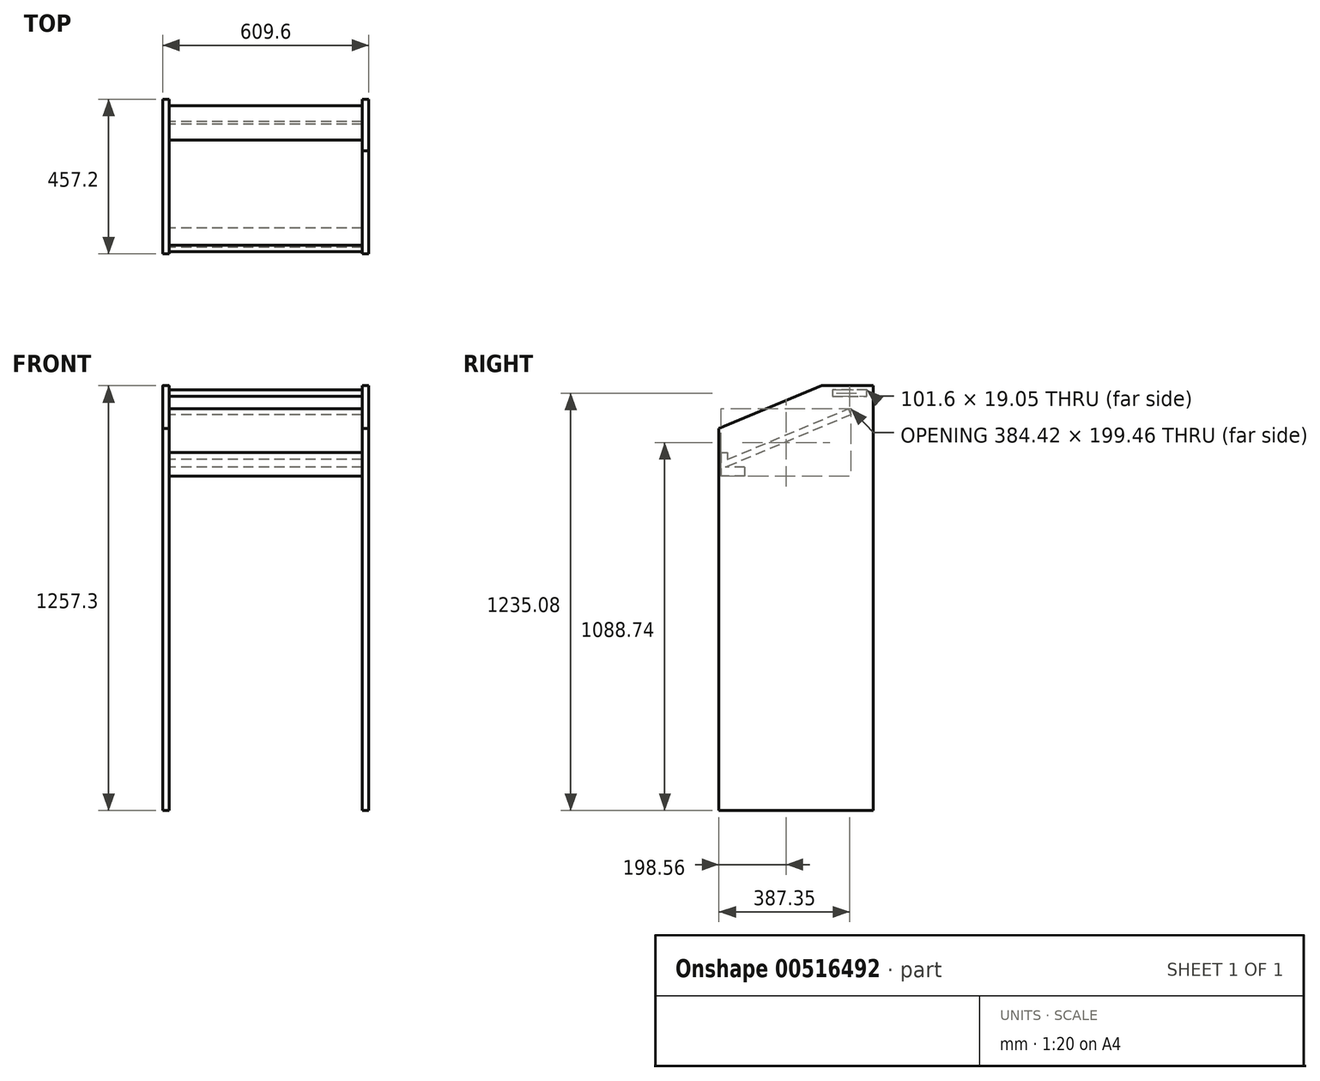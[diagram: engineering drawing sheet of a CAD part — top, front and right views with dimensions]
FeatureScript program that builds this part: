
annotation { "Feature Type Name" : "Feature", "Feature Type Description" : "" }
export const myFeature = defineFeature(function(context is Context, id is Id, definition is map)
    precondition{}
    {
        {
            var Q0;
            Q0=qCreatedBy(makeId("Right.planeOp"),FACE);
            var sketch = newSketch(context, id + "F0", { "sketchPlane" : qUnion([Q0])});
            skLineSegment(sketch, "E0.bottom", {"start": v(228.6, 628.65) * mm, "end": v(-228.6, 628.65) * mm});
            skLineSegment(sketch, "E0.top", {"start": v(228.6, -628.65) * mm, "end": v(-228.6, -628.65) * mm});
            skLineSegment(sketch, "E0.left", {"start": v(228.6, 628.65) * mm, "end": v(228.6, -628.65) * mm});
            skLineSegment(sketch, "E0.right", {"start": v(-228.6, 628.65) * mm, "end": v(-228.6, -628.65) * mm});
            skPoint(sketch, "E0.middle", {"position": v(0, 0) * mm});
            skLineSegment(sketch, "E1", {"start": v(-228.6, -628.65) * mm, "end": v(-228.6, 501.65) * mm});
            skLineSegment(sketch, "E2", {"start": v(228.6, 628.65) * mm, "end": v(81.28, 628.65) * mm});
            skLineSegment(sketch, "E3", {"start": v(71.51, 626.7) * mm, "end": v(-228.6, 501.65) * mm});
            skPoint(sketch, "E4.visualSharp", {"position": v(76.2, 628.65) * mm});
            skArc(sketch, "E4.filletArc", {"start": v(81.28, 628.65) * mm, "mid": v(76.3, 628.16) * mm, "end": v(71.51, 626.7) * mm});
            skSolve(sketch);
        }
        {
            var Q0;
            Q0=makeQuery(id+"F0.imprint","IMPRINT",FACE,{"disambiguationData":[TD([[makeQuery(id+"F0.imprint","IMPRINT",EDGE,{"derivedFrom":sQuery(id+"F0.wireOp",EDGE,"E0.top")}),-1.0]])]});
            extrude(context, id + "F1", {"entities" : qUnion([Q0]), "depth" : 19.05 * mm, "offsetDistance" : 25.4 * mm});
        }
        {
            var Q0;
            Q0=makeQuery(id+"F1.opExtrude","CAP_FACE",FACE,{"disambiguationData":[OSD([sQuery(id+"F0.wireOp",EDGE,"E0.top"),sQuery(id+"F0.wireOp",EDGE,"E0.left"),sQuery(id+"F0.wireOp",EDGE,"E1"),sQuery(id+"F0.wireOp",EDGE,"E2"),sQuery(id+"F0.wireOp",EDGE,"E3"),sQuery(id+"F0.wireOp",EDGE,"E4.filletArc")])],"isStart":false});
            var sketch = newSketch(context, id + "F2", { "sketchPlane" : qUnion([Q0])});
            skLineSegment(sketch, "E5", {"start": v(228.6, 628.65) * mm, "end": v(209.55, 628.65) * mm});
            skLineSegment(sketch, "E6", {"start": v(209.55, 615.95) * mm, "end": v(107.95, 615.95) * mm});
            skLineSegment(sketch, "E7", {"start": v(107.95, 615.95) * mm, "end": v(107.95, 596.9) * mm});
            skLineSegment(sketch, "E8", {"start": v(107.95, 596.9) * mm, "end": v(209.55, 596.9) * mm});
            skLineSegment(sketch, "E9", {"start": v(209.55, 596.9) * mm, "end": v(209.55, 615.95) * mm});
            skSolve(sketch);
        }
        {
            var Q0;
            Q0=makeQuery(id+"F2.imprint","IMPRINT",FACE,{"disambiguationData":[TD([[makeQuery(id+"F2.imprint","IMPRINT",EDGE,{"derivedFrom":sQuery(id+"F2.wireOp",EDGE,"E6")}),1.0]])]});
            extrude(context, id + "F3", {"entities" : qUnion([Q0]), "operationType" : NewBodyOperationType.ADD, "depth" : 571.5 * mm, "offsetDistance" : 25.4 * mm});
        }
        {
            var Q0;
            Q0=makeQuery(id+"F1.opExtrude","CAP_FACE",FACE,{"disambiguationData":[OSD([sQuery(id+"F0.wireOp",EDGE,"E0.top"),sQuery(id+"F0.wireOp",EDGE,"E0.left"),sQuery(id+"F0.wireOp",EDGE,"E1"),sQuery(id+"F0.wireOp",EDGE,"E2"),sQuery(id+"F0.wireOp",EDGE,"E3"),sQuery(id+"F0.wireOp",EDGE,"E4.filletArc")])],"isStart":false});
            var sketch = newSketch(context, id + "F4", { "sketchPlane" : qUnion([Q0])});
            skLineSegment(sketch, "E10", {"start": v(-228.6, 501.65) * mm, "end": v(-228.6, 400.05) * mm});
            skLineSegment(sketch, "E11", {"start": v(-228.6, 400.05) * mm, "end": v(107.95, 540.28) * mm});
            skLineSegment(sketch, "E12", {"start": v(107.95, 540.28) * mm, "end": v(154.84, 559.82) * mm});
            skLineSegment(sketch, "E13", {"start": v(154.84, 559.82) * mm, "end": v(162.17, 542.23) * mm});
            skLineSegment(sketch, "E14", {"start": v(162.17, 542.23) * mm, "end": v(-228.6, 379.41) * mm});
            skLineSegment(sketch, "E15", {"start": v(-228.6, 379.41) * mm, "end": v(-228.6, 430.21) * mm});
            skLineSegment(sketch, "E16", {"start": v(-228.6, 430.21) * mm, "end": v(-209.55, 430.21) * mm});
            skLineSegment(sketch, "E17", {"start": v(-209.55, 430.21) * mm, "end": v(-209.55, 379.41) * mm});
            skLineSegment(sketch, "E18", {"start": v(-209.55, 379.41) * mm, "end": v(-228.6, 379.41) * mm});
            skSolve(sketch);
        }
        {
            var Q0;
            {var subQ5=sQuery(id+"F4.wireOp",EDGE,"E16");Q0=makeQuery(id+"F4.imprint","IMPRINT",FACE,{"disambiguationData":[TD([[makeQuery(id+"F4.imprint","IMPRINT",EDGE,{"derivedFrom":subQ5}),-1.0]])]});}
            var Q1;
            {var subQ0=sQuery(id+"F4.wireOp",EDGE,"E15");var subQ1=sQuery(id+"F4.wireOp",EDGE,"E11");var subQ2=makeQuery(id+"F4.imprint","INTERSECT",VERTEX,{"derivedFrom":[subQ1,subQ0]});Q1=makeQuery(id+"F4.imprint","IMPRINT",FACE,{"disambiguationData":[TD([[makeQuery(id+"F4.imprint","IMPRINT",EDGE,{"disambiguationData":[TD([[subQ2,-1.0]])],"derivedFrom":subQ1}),-1.0]])]});}
            var Q2;
            {var subQ0=sQuery(id+"F4.wireOp",EDGE,"E18");Q2=makeQuery(id+"F4.imprint","IMPRINT",FACE,{"disambiguationData":[TD([[makeQuery(id+"F4.imprint","IMPRINT",EDGE,{"derivedFrom":subQ0}),-1.0]])]});}
            var Q3;
            {var subQ4=sQuery(id+"F4.wireOp",EDGE,"E12");Q3=makeQuery(id+"F4.imprint","IMPRINT",FACE,{"disambiguationData":[TD([[makeQuery(id+"F4.imprint","IMPRINT",EDGE,{"derivedFrom":subQ4}),-1.0]])]});}
            extrude(context, id + "F5", {"entities" : qUnion([Q0, Q1, Q2, Q3]), "operationType" : NewBodyOperationType.ADD, "depth" : 571.5 * mm, "offsetDistance" : 25.4 * mm});
        }
        {
            var Q0;
            Q0=makeQuery(id+"F5.boolean.opBoolean","MERGE",FACE,{"derivedFrom":[makeQuery(id+"F1.opExtrude","SWEPT_FACE",FACE,{"disambiguationData":[OSD([sQuery(id+"F0.wireOp",EDGE,"E1")])]}),makeQuery(id+"F5.opExtrude","SWEPT_FACE",FACE,{"disambiguationData":[OSD([sQuery(id+"F4.wireOp",EDGE,"E15")])]})]});
            var sketch = newSketch(context, id + "F6", { "sketchPlane" : qUnion([Q0])});
            skLineSegment(sketch, "E19", {"start": v(19.05, 430.21) * mm, "end": v(19.05, 379.41) * mm});
            skSolve(sketch);
        }
        {
            var Q0;
            Q0=makeQuery(id+"F6.imprint","IMPRINT",FACE,{"disambiguationData":[TD([[makeQuery(id+"F6.imprint","IMPRINT",EDGE,{"derivedFrom":sQuery(id+"F6.wireOp",EDGE,"E19")}),1.0]])]});
            extrude(context, id + "F7", {"entities" : qUnion([Q0]), "operationType" : NewBodyOperationType.REMOVE, "oppositeDirection" : true, "depth" : 6.35 * mm, "offsetDistance" : 25.4 * mm});
        }
        {
            var Q0;
            {var subQ0=sQuery(id+"F4.wireOp",EDGE,"E17");Q0=makeQuery(id+"F5.opExtrude","SWEPT_FACE",FACE,{"disambiguationData":[OSD([subQ0]),TDD([makeQuery(id+"F4.imprint","IMPRINT",EDGE,{"disambiguationData":[TD([[makeQuery(id+"F4.imprint","INTERSECT",VERTEX,{"derivedFrom":[sQuery(id+"F4.wireOp",EDGE,"E16"),subQ0]}),-1.0]])],"derivedFrom":subQ0})])]});}
            var Q1;
            {var subQ0=sQuery(id+"F4.wireOp",EDGE,"E17");Q1=makeQuery(id+"F5.opExtrude","SWEPT_FACE",FACE,{"disambiguationData":[OSD([subQ0]),TDD([makeQuery(id+"F4.imprint","IMPRINT",EDGE,{"disambiguationData":[TD([[makeQuery(id+"F4.imprint","INTERSECT",VERTEX,{"derivedFrom":[subQ0,sQuery(id+"F4.wireOp",EDGE,"E18")]}),1.0]])],"derivedFrom":subQ0})])]});}
            extrude(context, id + "F8", {"entities" : qUnion([Q0, Q1]), "operationType" : NewBodyOperationType.ADD, "depth" : 6.35 * mm, "offsetDistance" : 25.4 * mm});
        }
        {
            var Q0;
            Q0=makeQuery(id+"F3.opExtrude","CAP_FACE",FACE,{"disambiguationData":[OSD([sQuery(id+"F2.wireOp",EDGE,"E6"),sQuery(id+"F2.wireOp",EDGE,"E7"),sQuery(id+"F2.wireOp",EDGE,"E8"),sQuery(id+"F2.wireOp",EDGE,"E9")])],"isStart":false});
            var sketch = newSketch(context, id + "F9", { "sketchPlane" : qUnion([Q0])});
            skLineSegment(sketch, "E20", {"start": v(209.55, 628.65) * mm, "end": v(228.6, 628.65) * mm});
            skLineSegment(sketch, "E21", {"start": v(228.6, 628.65) * mm, "end": v(228.6, -628.65) * mm});
            skLineSegment(sketch, "E22", {"start": v(228.6, -628.65) * mm, "end": v(-228.6, -628.65) * mm});
            skLineSegment(sketch, "E23", {"start": v(-228.6, -628.65) * mm, "end": v(-228.6, 501.65) * mm});
            skLineSegment(sketch, "E24", {"start": v(228.6, 628.65) * mm, "end": v(76.2, 628.65) * mm});
            skLineSegment(sketch, "E25", {"start": v(76.2, 628.65) * mm, "end": v(-228.6, 501.65) * mm});
            skSolve(sketch);
        }
        {
            var Q0;
            {var subQ2=sQuery(id+"F9.wireOp",EDGE,"E21");Q0=makeQuery(id+"F9.imprint","IMPRINT",FACE,{"disambiguationData":[TD([[makeQuery(id+"F9.imprint","IMPRINT",EDGE,{"derivedFrom":subQ2}),-1.0]])]});}
            var Q1;
            Q1=makeQuery(id+"F9.imprint","IMPRINT",FACE,{"disambiguationData":[TD([[makeQuery(id+"F9.imprint","IMPRINT",EDGE,{"derivedFrom":makeQuery(id+"F3.opExtrude","CAP_EDGE",EDGE,{"disambiguationData":[OSD([sQuery(id+"F2.wireOp",EDGE,"E6")])],"isStart":false})}),1.0]])]});
            extrude(context, id + "F10", {"entities" : qUnion([Q0, Q1]), "operationType" : NewBodyOperationType.ADD, "depth" : 19.05 * mm, "offsetDistance" : 25.4 * mm});
        }
        {
            var Q0;
            {var subQ0=sQuery(id+"F4.wireOp",EDGE,"E18");Q0=makeQuery(id+"F8.boolean.opBoolean","MERGE",FACE,{"derivedFrom":[makeQuery(id+"F5.opExtrude","SWEPT_FACE",FACE,{"disambiguationData":[OSD([subQ0])]}),makeQuery(id+"F8.opExtrude","SWEPT_FACE",FACE,{"disambiguationData":[OSD([sQuery(id+"F4.wireOp",EDGE,"E17"),subQ0])]})]});}
            extrude(context, id + "F11", {"entities" : qUnion([Q0]), "operationType" : NewBodyOperationType.ADD, "depth" : 19.05 * mm, "offsetDistance" : 25.4 * mm});
        }
        {
            var Q0;
            {var subQ0=sQuery(id+"F4.wireOp",EDGE,"E18");var subQ1=sQuery(id+"F4.wireOp",EDGE,"E17");Q0=makeQuery(id+"F11.boolean.opBoolean","MERGE",FACE,{"derivedFrom":[makeQuery(id+"F8.opExtrude","CAP_FACE",FACE,{"disambiguationData":[OSD([subQ1]),TDD([makeQuery(id+"F5.opExtrude","SWEPT_FACE",FACE,{"disambiguationData":[OSD([subQ1]),TDD([makeQuery(id+"F4.imprint","IMPRINT",EDGE,{"disambiguationData":[TD([[makeQuery(id+"F4.imprint","INTERSECT",VERTEX,{"derivedFrom":[subQ1,subQ0]}),1.0]])],"derivedFrom":subQ1})])]})])],"isStart":false}),makeQuery(id+"F11.opExtrude","SWEPT_FACE",FACE,{"disambiguationData":[OSD([subQ1,subQ0]),TDD([makeQuery(id+"F8.opExtrude","CAP_EDGE",EDGE,{"disambiguationData":[OSD([subQ1,subQ0])],"isStart":false})])]})]});}
            extrude(context, id + "F12", {"entities" : qUnion([Q0]), "operationType" : NewBodyOperationType.ADD, "depth" : 50.8 * mm, "offsetDistance" : 25.4 * mm});
        }
    });
